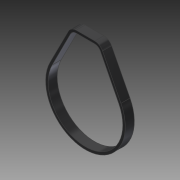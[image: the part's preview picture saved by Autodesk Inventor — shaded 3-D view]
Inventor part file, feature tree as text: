
AUTODESK INVENTOR PART (.ipt)
format: ipt  version: 2014 SP1 (Build 180222100, 222)  size: 97,792 bytes
history: native  units: in
note: dims shown in document units (in); Inventor stores cm internally (conversion verified against a paired STEP export)
features: reference x2, extrude x1, sketch x1
ambient origin geometry x8: Origin, YZ Plane, XZ Plane, XY Plane, X Axis, Y Axis, Z Axis, Center Point
bodies: Solid1 (feature_tree)
feature tree (4):
  extrude  "Extrusion1"  Depth=0.366in TaperAngle=0.0deg
  sketch  "Sketch1"  dims[d0=0.1in d1=0.366in d2=0.0in]
  reference  "Reference1"
  reference  "Reference2"
